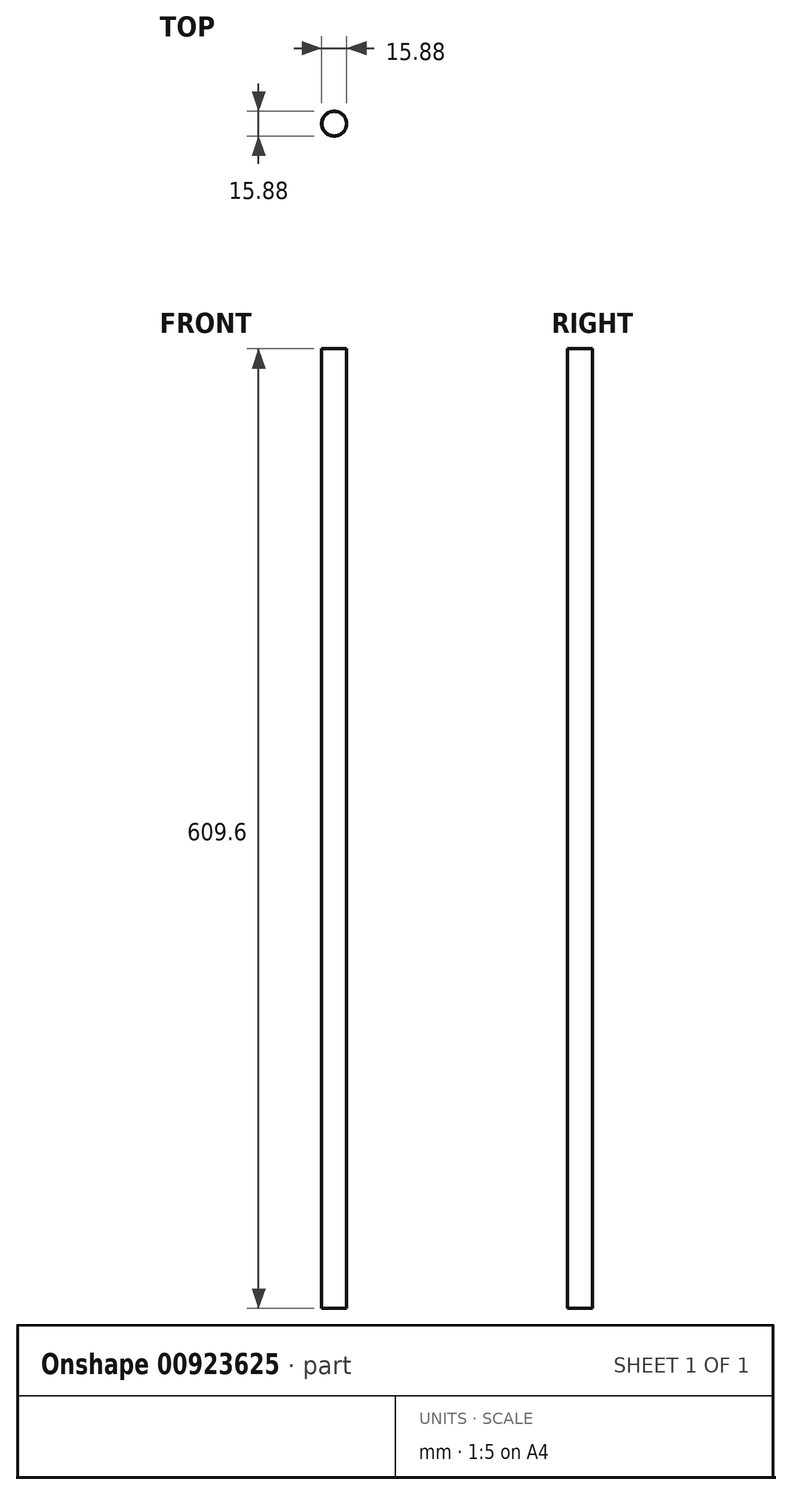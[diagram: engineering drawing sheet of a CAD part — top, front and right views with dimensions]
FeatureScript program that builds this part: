
annotation { "Feature Type Name" : "Feature", "Feature Type Description" : "" }
export const myFeature = defineFeature(function(context is Context, id is Id, definition is map)
    precondition{}
    {
        {
            var Q0;
            Q0=qCreatedBy(makeId("Top.planeOp"),FACE);
            var sketch = newSketch(context, id + "F0", { "sketchPlane" : qUnion([Q0])});
            skCircle(sketch, "E0", {"center": v(0, 0) * mm, "radius": 7.94 * mm});
            skCircle(sketch, "E1", {"center": v(0, 0) * mm, "radius": 7.81 * mm});
            skSolve(sketch);
        }
        {
            var Q0;
            Q0=sQuery(id+"F0.wireOp",EDGE,"E0");
            var Q1;
            Q1=sQuery(id+"F0.wireOp",EDGE,"E1");
            extrude(context, id + "F1", {"bodyType" : ToolBodyType.SURFACE, "surfaceEntities" : qUnion([Q0, Q1]), "depth" : 609.6 * mm, "offsetDistance" : 25.4 * mm});
        }
    });
